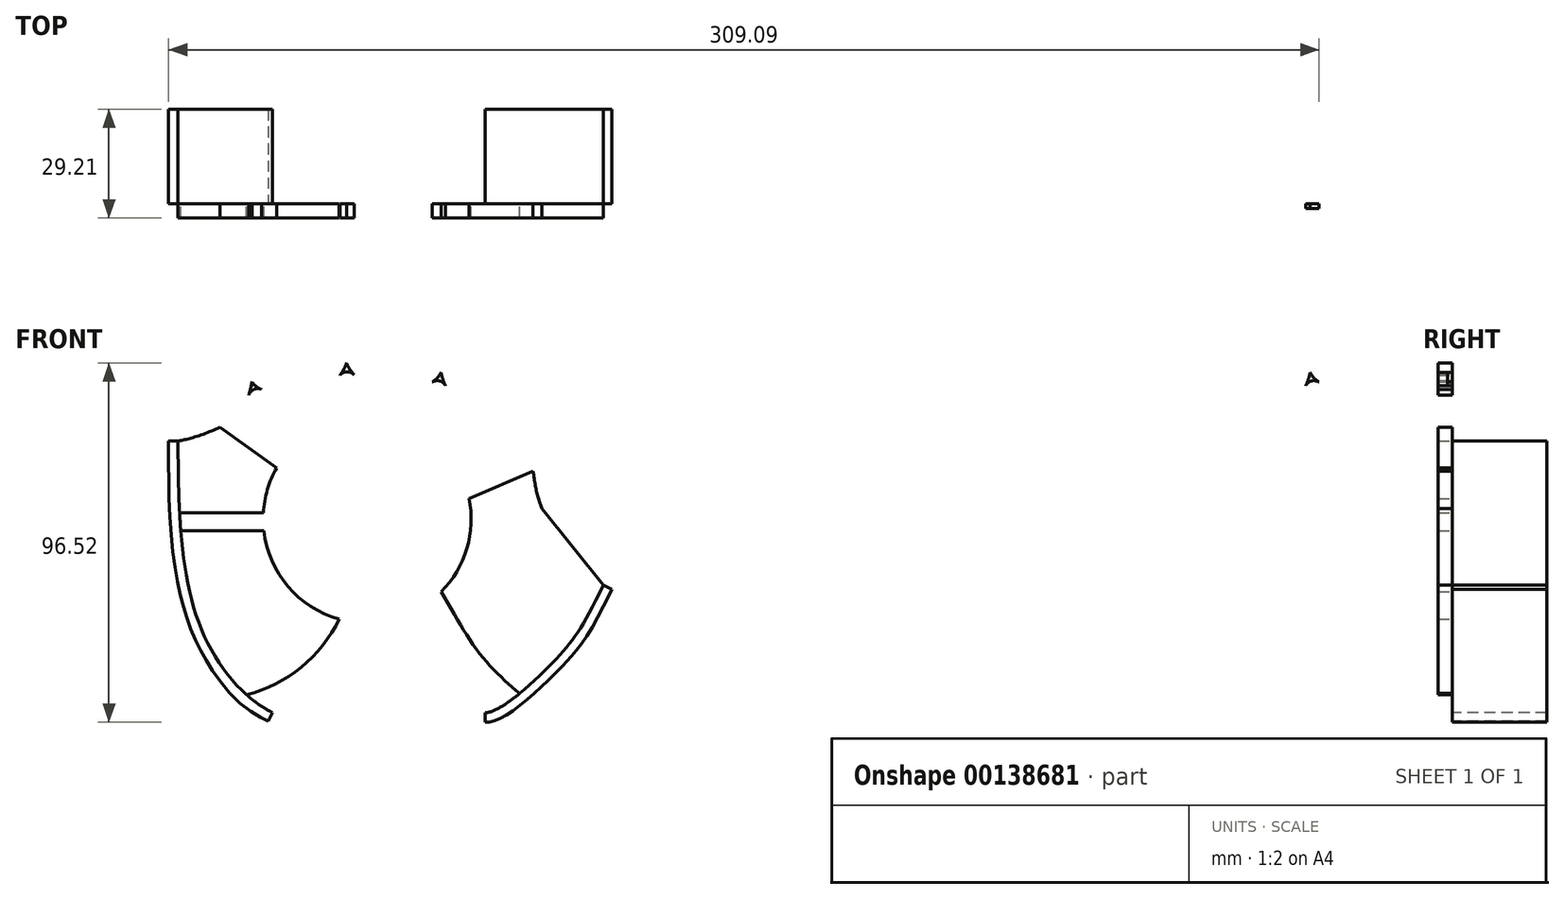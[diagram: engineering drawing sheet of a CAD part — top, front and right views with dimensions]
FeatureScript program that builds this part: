
annotation { "Feature Type Name" : "Feature", "Feature Type Description" : "" }
export const myFeature = defineFeature(function(context is Context, id is Id, definition is map)
    precondition{}
    {
        {
            var Q0;
            Q0=qCreatedBy(makeId("Front.planeOp"),FACE);
            var sketch = newSketch(context, id + "F0", { "sketchPlane" : qUnion([Q0])});
            skCircle(sketch, "E0", {"center": v(0, 0) * mm, "radius": 15.88 * mm});
            skCircle(sketch, "E1", {"center": v(0, 0) * mm, "radius": 22.86 * mm});
            skLineSegment(sketch, "E2", {"start": v(-25.4, -52.07) * mm, "end": v(31.75, -52.07) * mm});
            skFitSpline(sketch, "E3", {"points": [v(-25.4, -52.07) * mm, v(-44.45, -29.84) * mm, v(-50.8, 20.96) * mm], "startDerivative": vector(-55.54, 27.96) * mm, "endDerivative": vector(0, 110.4) * mm});
            skFitSpline(sketch, "E4", {"points": [v(31.75, -52.07) * mm, v(50.04, -38.4) * mm, v(63.5, -17.78) * mm], "startDerivative": vector(25.44, 0) * mm, "endDerivative": vector(34.74, 69.25) * mm});
            skLineSegment(sketch, "E5", {"start": v(63.5, -17.78) * mm, "end": v(46.99, 2.86) * mm});
            skFitSpline(sketch, "E6", {"points": [v(46.99, 2.86) * mm, v(44.76, 11.63) * mm, v(43.81, 26.67) * mm], "startDerivative": vector(-7.75, 15.3) * mm, "endDerivative": vector(0.62, 31.7) * mm});
            skFitSpline(sketch, "E7", {"points": [v(-50.8, 20.96) * mm, v(-36.52, 26.5) * mm, v(-30.96, 36.83) * mm], "startDerivative": vector(14.6, 2.03) * mm, "endDerivative": vector(5.37, 27.73) * mm});
            skFitSpline(sketch, "E8", {"points": [v(-30.96, 36.83) * mm, v(-17.8, 34.17) * mm, v(-5.56, 41.91) * mm], "startDerivative": vector(12.02, -18.86) * mm, "endDerivative": vector(9.87, 31.06) * mm});
            skFitSpline(sketch, "E9", {"points": [v(-5.56, 41.91) * mm, v(6.2, 34.79) * mm, v(19.84, 39.37) * mm], "startDerivative": vector(12.54, -29.56) * mm, "endDerivative": vector(10.19, 22.75) * mm});
            skFitSpline(sketch, "E10", {"points": [v(19.84, 39.37) * mm, v(26.65, 30.6) * mm, v(43.81, 26.67) * mm], "startDerivative": vector(6.38, -30.04) * mm, "endDerivative": vector(32, -6.3) * mm});
            skArc(sketch, "E11.filletArc", {"start": v(-28.4, 34.83) * mm, "mid": v(-30.46, 34.8) * mm, "end": v(-31.82, 33.25) * mm});
            skArc(sketch, "E12.filletArc", {"start": v(-3.53, 38.72) * mm, "mid": v(-5.45, 39.54) * mm, "end": v(-7.34, 38.64) * mm});
            skArc(sketch, "E13.filletArc", {"start": v(21.07, 35.8) * mm, "mid": v(19.49, 37.08) * mm, "end": v(17.46, 36.79) * mm});
            skLineSegment(sketch, "E14", {"start": v(-117.4, -89.45) * mm, "end": v(136.6, -89.45) * mm});
            skLineSegment(sketch, "E15", {"start": v(136.6, -89.45) * mm, "end": v(136.6, 75.65) * mm});
            skArc(sketch, "E16.MirrorCS", {"start": v(252.14, 35.8) * mm, "mid": v(253.72, 37.08) * mm, "end": v(255.75, 36.79) * mm});
            skArc(sketch, "E17.MirrorCS", {"start": v(301.62, 34.83) * mm, "mid": v(303.68, 34.8) * mm, "end": v(305.03, 33.25) * mm});
            skArc(sketch, "E18.MirrorCS", {"start": v(276.74, 38.72) * mm, "mid": v(278.66, 39.54) * mm, "end": v(280.55, 38.64) * mm});
            skFitSpline(sketch, "E19.MirrorCS", {"points": [v(304.17, 36.83) * mm, v(291.01, 34.17) * mm, v(278.77, 41.91) * mm], "startDerivative": vector(-12.02, -18.86) * mm, "endDerivative": vector(-9.87, 31.06) * mm});
            skFitSpline(sketch, "E20.MirrorCS", {"points": [v(278.77, 41.91) * mm, v(267.02, 34.79) * mm, v(253.37, 39.37) * mm], "startDerivative": vector(-12.54, -29.56) * mm, "endDerivative": vector(-10.19, 22.75) * mm});
            skFitSpline(sketch, "E21.MirrorCS", {"points": [v(253.37, 39.37) * mm, v(246.56, 30.6) * mm, v(229.4, 26.67) * mm], "startDerivative": vector(-6.38, -30.04) * mm, "endDerivative": vector(-32, -6.3) * mm});
            skFitSpline(sketch, "E22.MirrorCS", {"points": [v(324.01, 20.96) * mm, v(309.73, 26.5) * mm, v(304.17, 36.83) * mm], "startDerivative": vector(-14.6, 2.03) * mm, "endDerivative": vector(-5.37, 27.73) * mm});
            skFitSpline(sketch, "E23.MirrorCS", {"points": [v(226.22, 2.86) * mm, v(228.45, 11.63) * mm, v(229.4, 26.67) * mm], "startDerivative": vector(7.75, 15.3) * mm, "endDerivative": vector(-0.62, 31.7) * mm});
            skCircle(sketch, "E24.MirrorC", {"center": v(273.21, 0) * mm, "radius": 15.88 * mm});
            skLineSegment(sketch, "E25.MirrorCS", {"start": v(298.61, -52.07) * mm, "end": v(241.46, -52.07) * mm});
            skFitSpline(sketch, "E26.MirrorCS", {"points": [v(241.46, -52.07) * mm, v(223.17, -38.4) * mm, v(209.71, -17.78) * mm], "startDerivative": vector(-25.44, 0) * mm, "endDerivative": vector(-34.74, 69.25) * mm});
            skLineSegment(sketch, "E27.MirrorCS", {"start": v(209.71, -17.78) * mm, "end": v(226.22, 2.86) * mm});
            skFitSpline(sketch, "E28.MirrorCS", {"points": [v(298.61, -52.07) * mm, v(317.66, -29.84) * mm, v(324.01, 20.96) * mm], "startDerivative": vector(55.54, 27.96) * mm, "endDerivative": vector(0, 110.4) * mm});
            skCircle(sketch, "E29.MirrorC", {"center": v(273.21, 0) * mm, "radius": 22.86 * mm});
            skCircle(sketch, "E30", {"center": v(18.13, -210.06) * mm, "radius": 15.88 * mm});
            skCircle(sketch, "E31", {"center": v(18.13, -210.06) * mm, "radius": 22.86 * mm});
            skLineSegment(sketch, "E32", {"start": v(-7.27, -262.13) * mm, "end": v(49.88, -262.13) * mm});
            skFitSpline(sketch, "E33", {"points": [v(-7.27, -262.13) * mm, v(-26.32, -239.9) * mm, v(-32.67, -189.1) * mm], "startDerivative": vector(-55.54, 27.96) * mm, "endDerivative": vector(0, 110.4) * mm});
            skFitSpline(sketch, "E34", {"points": [v(49.88, -262.13) * mm, v(68.17, -248.46) * mm, v(81.63, -227.84) * mm], "startDerivative": vector(23.96, 8.57) * mm, "endDerivative": vector(34.74, 69.25) * mm});
            skLineSegment(sketch, "E35", {"start": v(81.63, -227.84) * mm, "end": v(65.12, -207.2) * mm});
            skFitSpline(sketch, "E36", {"points": [v(65.12, -207.2) * mm, v(62.88, -198.44) * mm, v(61.94, -183.4) * mm], "startDerivative": vector(-7.75, 15.3) * mm, "endDerivative": vector(0.62, 31.7) * mm});
            skFitSpline(sketch, "E37", {"points": [v(-32.67, -189.1) * mm, v(-18.4, -183.56) * mm, v(-12.83, -173.23) * mm], "startDerivative": vector(14.6, 2.03) * mm, "endDerivative": vector(5.37, 27.73) * mm});
            skFitSpline(sketch, "E38", {"points": [v(-12.83, -173.23) * mm, v(0.32, -175.9) * mm, v(12.57, -168.15) * mm], "startDerivative": vector(12.02, -18.86) * mm, "endDerivative": vector(9.87, 31.06) * mm});
            skFitSpline(sketch, "E39", {"points": [v(12.57, -168.15) * mm, v(24.32, -175.28) * mm, v(37.97, -170.7) * mm], "startDerivative": vector(12.54, -29.56) * mm, "endDerivative": vector(10.19, 22.75) * mm});
            skFitSpline(sketch, "E40", {"points": [v(37.97, -170.7) * mm, v(44.78, -179.47) * mm, v(61.94, -183.4) * mm], "startDerivative": vector(6.38, -30.04) * mm, "endDerivative": vector(32, -6.3) * mm});
            skArc(sketch, "E41.filletArc", {"start": v(-10.28, -175.24) * mm, "mid": v(-12.34, -175.27) * mm, "end": v(-13.7, -176.81) * mm});
            skArc(sketch, "E42.filletArc", {"start": v(14.6, -171.34) * mm, "mid": v(12.67, -170.52) * mm, "end": v(10.79, -171.42) * mm});
            skArc(sketch, "E43.filletArc", {"start": v(39.2, -174.27) * mm, "mid": v(37.61, -172.98) * mm, "end": v(35.59, -173.27) * mm});
            skCircle(sketch, "E44", {"center": v(0, 0) * mm, "radius": 24.13 * mm});
            skArc(sketch, "E45", {"start": v(19.91, -19.6) * mm, "mid": v(-18.45, 20.98) * mm, "end": v(16.89, -22.26) * mm});
            skFitSpline(sketch, "E46", {"points": [v(15, -18.9) * mm, v(27.46, -38.77) * mm, v(37.97, -49.2) * mm], "startDerivative": vector(21.9, -38.89) * mm, "endDerivative": vector(23.4, -19.85) * mm});
            skFitSpline(sketch, "E47", {"points": [v(19.91, -19.6) * mm, v(30.6, -36.63) * mm, v(40.95, -46.9) * mm], "startDerivative": vector(20.81, -35.48) * mm, "endDerivative": vector(22.55, -19.57) * mm});
            skLineSegment(sketch, "E48", {"start": v(-24.33, 13.73) * mm, "end": v(-39.56, 24.69) * mm});
            skLineSegment(sketch, "E49", {"start": v(14.76, 35.6) * mm, "end": v(9.54, 26.26) * mm});
            skLineSegment(sketch, "E50", {"start": v(-27.76, -3.17) * mm, "end": v(-50.08, -3.17) * mm});
            skLineSegment(sketch, "E51", {"start": v(-50.4, 1.6) * mm, "end": v(-27.9, 1.6) * mm});
            skLineSegment(sketch, "E52", {"start": v(-22.07, 17.13) * mm, "end": v(-35.4, 27.41) * mm});
            skLineSegment(sketch, "E53", {"start": v(5.04, 34.9) * mm, "end": v(5.04, 27.48) * mm});
            skLineSegment(sketch, "E54", {"start": v(27.39, 5.53) * mm, "end": v(44.76, 12.94) * mm});
            skLineSegment(sketch, "E55", {"start": v(26.13, 9.88) * mm, "end": v(44.08, 17.54) * mm});
            skArc(sketch, "E56", {"start": v(-32.4, -47.25) * mm, "mid": v(-17.7, -39.85) * mm, "end": v(-7.52, -26.9) * mm});
            skLineSegment(sketch, "E57", {"start": v(-3.17, -45.02) * mm, "end": v(3.18, -45.02) * mm});
            skLineSegment(sketch, "E58", {"start": v(3.18, -45.02) * mm, "end": v(6.99, -52.07) * mm});
            skLineSegment(sketch, "E59", {"start": v(-3.17, -45.02) * mm, "end": v(-6.98, -52.07) * mm});
            skFitSpline(sketch, "E60.0", {"points": [v(-26.54, -54.34) * mm, v(-29.06, -53.07) * mm, v(-33.85, -49.8) * mm, v(-39.04, -44.22) * mm, v(-42.63, -39.04) * mm, v(-45.01, -34.84) * mm, v(-47.06, -30.35) * mm, v(-48.75, -25.64) * mm, v(-50.1, -20.7) * mm, v(-51.52, -13.8) * mm, v(-52.66, -4.59) * mm, v(-53.26, 7.52) * mm, v(-53.34, 16.34) * mm, v(-53.34, 20.95) * mm]});
            skLineSegment(sketch, "E61", {"start": v(-50.8, 20.95) * mm, "end": v(-53.34, 20.95) * mm});
            skFitSpline(sketch, "E62.0", {"points": [v(31.75, -54.6) * mm, v(32.23, -54.6) * mm, v(33.13, -54.5) * mm, v(34.42, -54.11) * mm, v(35.68, -53.57) * mm, v(37.38, -52.66) * mm, v(39.55, -51.24) * mm, v(42.23, -49.18) * mm, v(44.93, -46.88) * mm, v(47.55, -44.46) * mm, v(49.6, -42.46) * mm, v(51.13, -40.93) * mm, v(52.2, -39.83) * mm, v(53.19, -38.79) * mm, v(54.42, -37.44) * mm, v(55.84, -35.79) * mm, v(57.4, -33.76) * mm, v(59.4, -30.86) * mm, v(61.88, -26.58) * mm, v(64.32, -21.81) * mm, v(65.77, -18.92) * mm]});
            skLineSegment(sketch, "E63", {"start": v(-26.54, -54.34) * mm, "end": v(-25.4, -52.07) * mm});
            skLineSegment(sketch, "E64", {"start": v(31.75, -52.07) * mm, "end": v(31.75, -54.6) * mm});
            skLineSegment(sketch, "E65", {"start": v(63.5, -17.78) * mm, "end": v(65.77, -18.92) * mm});
            skSolve(sketch);
        }
        {
            var Q0;
            Q0=makeQuery(id+"F0.imprint","IMPRINT",FACE,{"disambiguationData":[TD([[makeQuery(id+"F0.imprint","IMPRINT",EDGE,{"derivedFrom":sQuery(id+"F0.wireOp",EDGE,"E8")}),-1.0]])]});
            var Q1;
            {var subQ1=sQuery(id+"F0.wireOp",EDGE,"E10");Q1=makeQuery(id+"F0.imprint","IMPRINT",FACE,{"disambiguationData":[TD([[makeQuery(id+"F0.imprint","IMPRINT",EDGE,{"derivedFrom":subQ1}),-1.0]])]});}
            var Q2;
            {var subQ0=sQuery(id+"F0.wireOp",EDGE,"E48");Q2=makeQuery(id+"F0.imprint","IMPRINT",FACE,{"disambiguationData":[TD([[makeQuery(id+"F0.imprint","IMPRINT",EDGE,{"derivedFrom":subQ0}),1.0]])]});}
            var Q3;
            {var subQ0=sQuery(id+"F0.wireOp",EDGE,"E50");Q3=makeQuery(id+"F0.imprint","IMPRINT",FACE,{"disambiguationData":[TD([[makeQuery(id+"F0.imprint","IMPRINT",EDGE,{"derivedFrom":subQ0}),1.0]])]});}
            var Q4;
            {var subQ1=sQuery(id+"F0.wireOp",EDGE,"E5");Q4=makeQuery(id+"F0.imprint","IMPRINT",FACE,{"disambiguationData":[TD([[makeQuery(id+"F0.imprint","IMPRINT",EDGE,{"derivedFrom":subQ1}),1.0]])]});}
            extrude(context, id + "F1", {"entities" : qUnion([Q0, Q1, Q2, Q3, Q4]), "depth" : 3.8 * mm});
        }
        {
            var Q0;
            Q0=makeQuery(id+"F0.imprint","IMPRINT",FACE,{"disambiguationData":[TD([[makeQuery(id+"F0.imprint","IMPRINT",EDGE,{"derivedFrom":sQuery(id+"F0.wireOp",EDGE,"E60.0")}),-1.0]])]});
            var Q1;
            Q1=makeQuery(id+"F0.imprint","IMPRINT",FACE,{"disambiguationData":[TD([[makeQuery(id+"F0.imprint","IMPRINT",EDGE,{"derivedFrom":sQuery(id+"F0.wireOp",EDGE,"E62.0")}),1.0]])]});
            extrude(context, id + "F2", {"entities" : qUnion([Q0, Q1]), "oppositeDirection" : true, "depth" : 25.4 * mm});
        }
        {
            var Q0;
            Q0=makeQuery(id+"F0.imprint","IMPRINT",FACE,{"disambiguationData":[TD([[makeQuery(id+"F0.imprint","IMPRINT",EDGE,{"derivedFrom":sQuery(id+"F0.wireOp",EDGE,"E16.MirrorCS")}),-1.0]])]});
            extrude(context, id + "F3", {"entities" : qUnion([Q0]), "depth" : 1.27 * mm});
        }
    });
